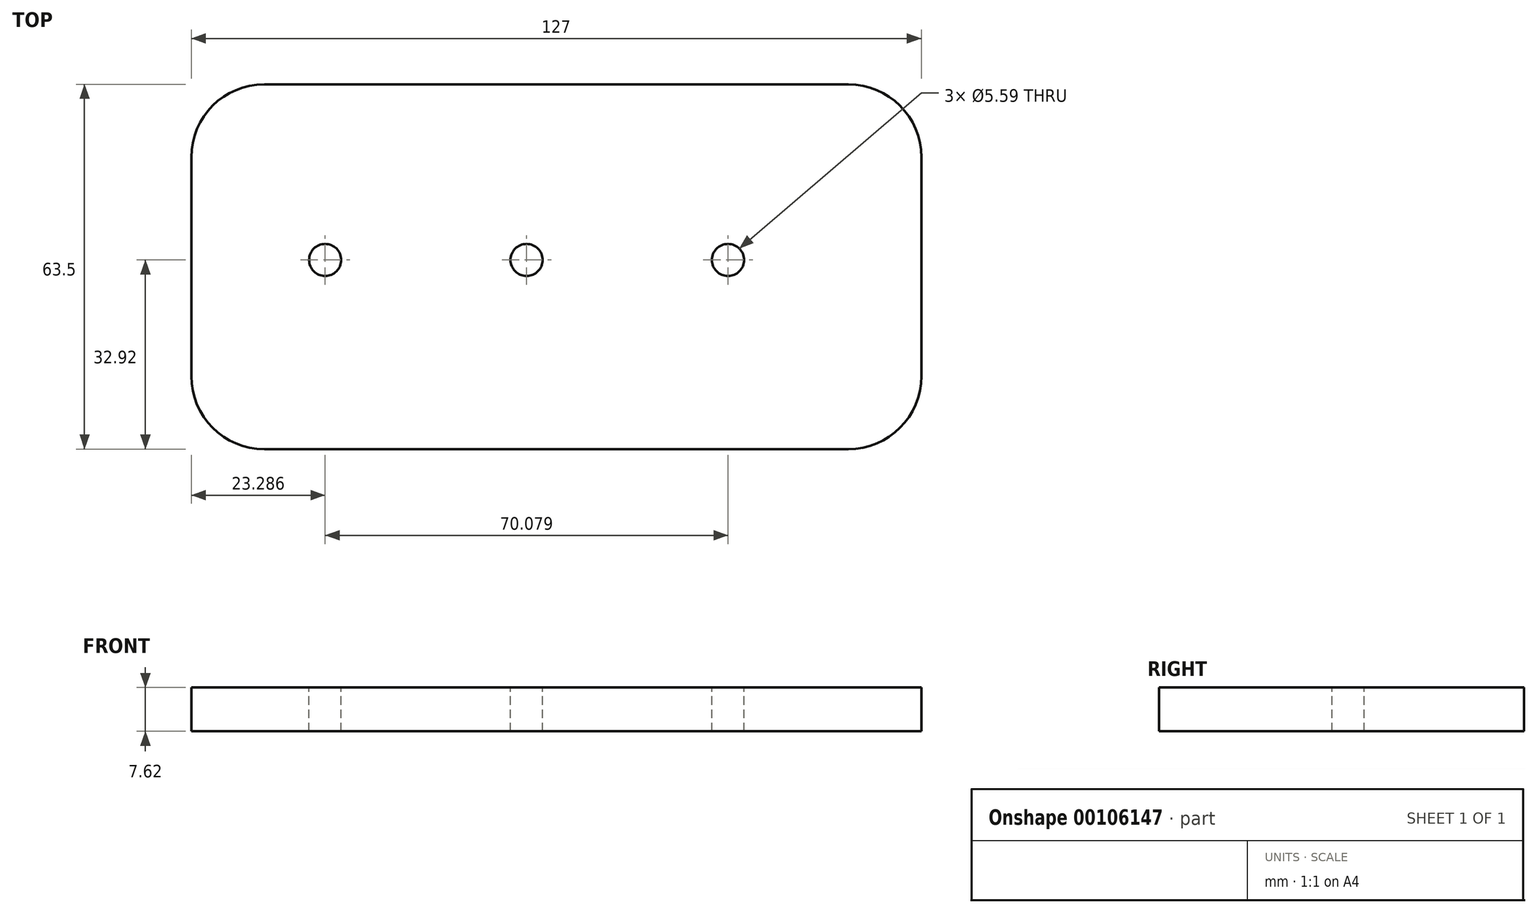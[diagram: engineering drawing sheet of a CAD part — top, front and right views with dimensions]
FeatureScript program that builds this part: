
annotation { "Feature Type Name" : "Feature", "Feature Type Description" : "" }
export const myFeature = defineFeature(function(context is Context, id is Id, definition is map)
    precondition{}
    {
        {
            var Q0;
            Q0=qCreatedBy(makeId("Top.planeOp"),FACE);
            var sketch = newSketch(context, id + "F0", { "sketchPlane" : qUnion([Q0])});
            skLineSegment(sketch, "E0.bottom", {"start": v(-61.2, 30.58) * mm, "end": v(65.8, 30.58) * mm});
            skLineSegment(sketch, "E0.top", {"start": v(-61.2, -32.92) * mm, "end": v(65.8, -32.92) * mm});
            skLineSegment(sketch, "E0.left", {"start": v(-61.2, 30.58) * mm, "end": v(-61.2, -32.92) * mm});
            skLineSegment(sketch, "E0.right", {"start": v(65.8, 30.58) * mm, "end": v(65.8, -32.92) * mm});
            skSolve(sketch);
        }
        {
            var Q0;
            Q0=makeQuery(id+"F0.imprint","IMPRINT",FACE,{"disambiguationData":[TD([[makeQuery(id+"F0.imprint","IMPRINT",EDGE,{"derivedFrom":sQuery(id+"F0.wireOp",EDGE,"E0.bottom")}),-1.0]])]});
            extrude(context, id + "F1", {"entities" : qUnion([Q0]), "depth" : 7.62 * mm});
        }
        {
            var Q0;
            Q0=makeQuery(id+"F1.opExtrude","CAP_FACE",FACE,{"disambiguationData":[OSD([sQuery(id+"F0.wireOp",EDGE,"E0.bottom"),sQuery(id+"F0.wireOp",EDGE,"E0.top"),sQuery(id+"F0.wireOp",EDGE,"E0.left"),sQuery(id+"F0.wireOp",EDGE,"E0.right")])],"isStart":false});
            var sketch = newSketch(context, id + "F2", { "sketchPlane" : qUnion([Q0])});
            skCircle(sketch, "E1", {"center": v(-2.87, 0) * mm, "radius": 2.8 * mm});
            skCircle(sketch, "E2", {"center": v(32.16, 0) * mm, "radius": 2.8 * mm});
            skCircle(sketch, "E3", {"center": v(-37.91, 0) * mm, "radius": 2.8 * mm});
            skSolve(sketch);
        }
        {
            var Q0;
            Q0=makeQuery(id+"F2.imprint","IMPRINT",FACE,{"disambiguationData":[TD([[makeQuery(id+"F2.imprint","IMPRINT",EDGE,{"derivedFrom":sQuery(id+"F2.wireOp",EDGE,"E1")}),1.0]])]});
            var Q1;
            Q1=makeQuery(id+"F2.imprint","IMPRINT",FACE,{"disambiguationData":[TD([[makeQuery(id+"F2.imprint","IMPRINT",EDGE,{"derivedFrom":sQuery(id+"F2.wireOp",EDGE,"E2")}),1.0]])]});
            var Q2;
            Q2=makeQuery(id+"F2.imprint","IMPRINT",FACE,{"disambiguationData":[TD([[makeQuery(id+"F2.imprint","IMPRINT",EDGE,{"derivedFrom":sQuery(id+"F2.wireOp",EDGE,"E3")}),1.0]])]});
            extrude(context, id + "F3", {"entities" : qUnion([Q0, Q1, Q2]), "operationType" : NewBodyOperationType.REMOVE, "oppositeDirection" : true, "depth" : 7.62 * mm});
        }
        {
            var Q0;
            Q0=makeQuery(id+"F1.opExtrude","SWEPT_EDGE",EDGE,{"disambiguationData":[OSD([sQuery(id+"F0.wireOp",EDGE,"E0.top"),sQuery(id+"F0.wireOp",EDGE,"E0.right")])]});
            var Q1;
            Q1=makeQuery(id+"F1.opExtrude","SWEPT_EDGE",EDGE,{"disambiguationData":[OSD([sQuery(id+"F0.wireOp",EDGE,"E0.top"),sQuery(id+"F0.wireOp",EDGE,"E0.left")])]});
            var Q2;
            Q2=makeQuery(id+"F1.opExtrude","SWEPT_EDGE",EDGE,{"disambiguationData":[OSD([sQuery(id+"F0.wireOp",EDGE,"E0.bottom"),sQuery(id+"F0.wireOp",EDGE,"E0.right")])]});
            var Q3;
            Q3=makeQuery(id+"F1.opExtrude","SWEPT_EDGE",EDGE,{"disambiguationData":[OSD([sQuery(id+"F0.wireOp",EDGE,"E0.bottom"),sQuery(id+"F0.wireOp",EDGE,"E0.left")])]});
            fillet(context, id + "F4", {"entities" : qUnion([Q0, Q1, Q2, Q3]), "radius" : 12.7 * mm, "tangentPropagation" : true, "allowEdgeOverflow" : false});
        }
    });
